# Revit family: STXC612LRLGUU2BTMRSWCT
name_source: partatom
category: Lighting Fixtures
units: mm (PartAtom-declared; Revit-internal decimal feet)

## family parameters
Always vertical = Yes
Cut with Voids When Loaded = No
Host = Wall
Light Source = Yes
Maintain Annotation Orientation = No
Part Type = Normal
Room Calculation Point = No
Round Connector Dimension = Use Diameter
Shared = No

## types (2) — shared parameters
Color Filter = 16777215
Default Elevation = 0.00"
Dimming Lamp Color Temperature Shift = <None>
Emit from Line Length = 24.00"
HOUSING MATERIAL = HOUSING MATERIAL
LENS MATERIAL = LENS MATERIAL
Lamp = LED
Manufacturer = BEGHELLI
Model = STXC CT
Type Image = STXC CT - IMAGE.jpg
Wattage Comments = 1W

## per-type parameters (varying)
| type | LETTER MATERIAL | MOUNTING HEIGHT | Photometric Web File | Tilt Angle |
| STXC6-12LGUU2BTMRSWCT | LETTERS MATERIAL GREEN | 92.94" | generic | 60.00° |
| STXC6-12LRUU2BTMRSWCT | LETTERS MATERIAL RED | 90.00" | MR16 LED_7W-12-24V.ies | 0.00° |

## geometry (parser evidence)
native form markers: Sweep x13
no freeform markers — native parametric forms only
